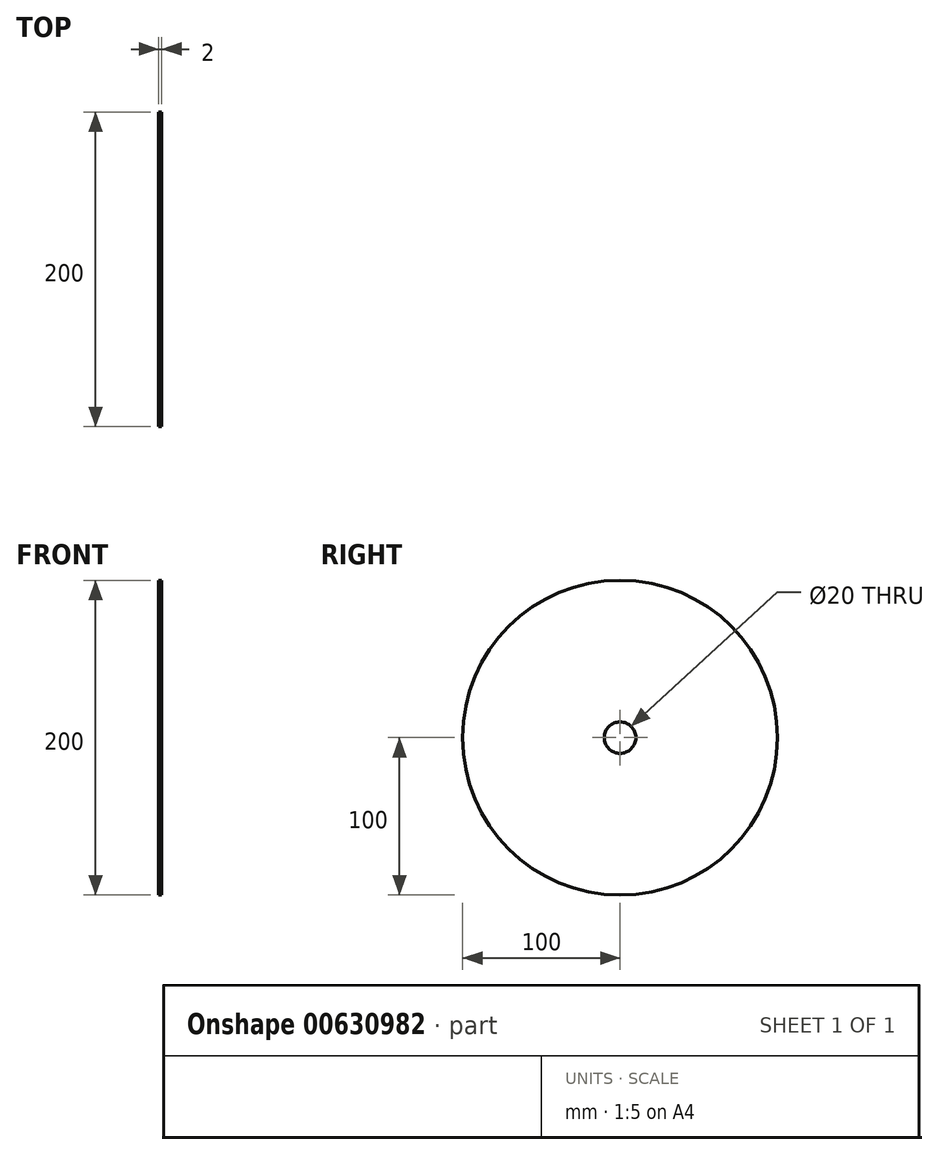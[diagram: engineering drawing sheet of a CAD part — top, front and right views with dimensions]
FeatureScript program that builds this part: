
annotation { "Feature Type Name" : "Feature", "Feature Type Description" : "" }
export const myFeature = defineFeature(function(context is Context, id is Id, definition is map)
    precondition{}
    {
        {
            var Q0;
            Q0=qCreatedBy(makeId("Right.planeOp"),FACE);
            var sketch = newSketch(context, id + "F0", { "sketchPlane" : qUnion([Q0])});
            skCircle(sketch, "E0", {"center": v(0, 0) * mm, "radius": 10 * mm});
            skCircle(sketch, "E1", {"center": v(0, 0) * mm, "radius": 100 * mm});
            skSolve(sketch);
        }
        {
            var Q0;
            Q0 = qSketchRegion(id + "F0", true);
            extrude(context, id + "F1", {"entities" : qUnion([Q0]), "depth" : 2 * mm, "offsetDistance" : 25 * mm});
        }
    });
